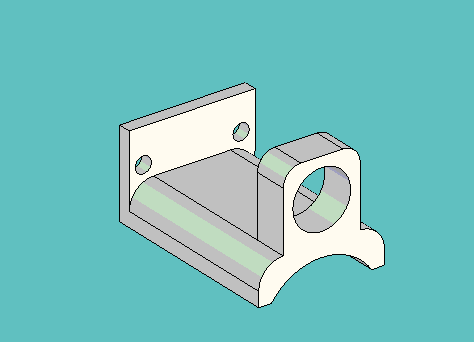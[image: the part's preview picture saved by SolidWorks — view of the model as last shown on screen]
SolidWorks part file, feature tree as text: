
SOLIDWORKS PART (.sldprt)
format: sldprt  version: not decoded by parser v0  size: 422,912 bytes
history: native  units: mm
features: sketch x6, extrude x3, material x1, cut_extrude x1, fillet x1 (+11 scaffold rows collapsed)
feature tree (23):
  scaffold x11  (default folders/planes/origin — collapsed)
  material  "Material <not specified>"
  sketch  "Sketch1"  dims[D1=~2.38125mm D2=~2.38125mm D3=6.35mm D4=11.1125mm D5=15.875mm D6=25.4mm]
  sketch  "Sketch6"  dims[c1.D3=9.525mm c1.D5=22.225mm c1.D1=22.86mm c1.D2=11.1125mm c1.D4=22.86mm c2.D2=11.1125mm c2.D3=11.43mm c2.D5=22.86mm c2.D6=4.7625mm]
  extrude  "Extrude3"  Depth=2.38125mm
  sketch  "Sketch7"  dims[c1.D4=7.62mm c1.D1=~2.38125mm c1.D2=4.7625mm c1.D3=8.89mm c2.D1=~2.38125mm]
  extrude  "Extrude4"  Depth=36.1188mm
  sketch  "Sketch2"  dims[c1.D2=10.4902mm c1.D3=9.525mm c1.D4=7.9375mm c1.D5=7.9375mm c1.D1=14.2875mm c2.D3=~7.14375mm c2.D1=~7.14375mm c3.D3=14.2875mm c3.D1=0.0mm]
  extrude  "Extrude5"  Depth=10.7188mm
  sketch  "Sketch4"  dims[D1=2.9464mm D2=2.9464mm]
  cut_extrude  "Cut-Extrude3"  [1 undecoded]
  fillet  "Fillet4"  Radius=3.175mm
  sketch  "Sketch8"
decode coverage: 9 of 11 modeling features carry decoded parameters
note: ~ marks probable driven/reference dimensions
note: 1 parameter value undecoded
note: suppression state not decoded; provenance and decode notes live in map.json
